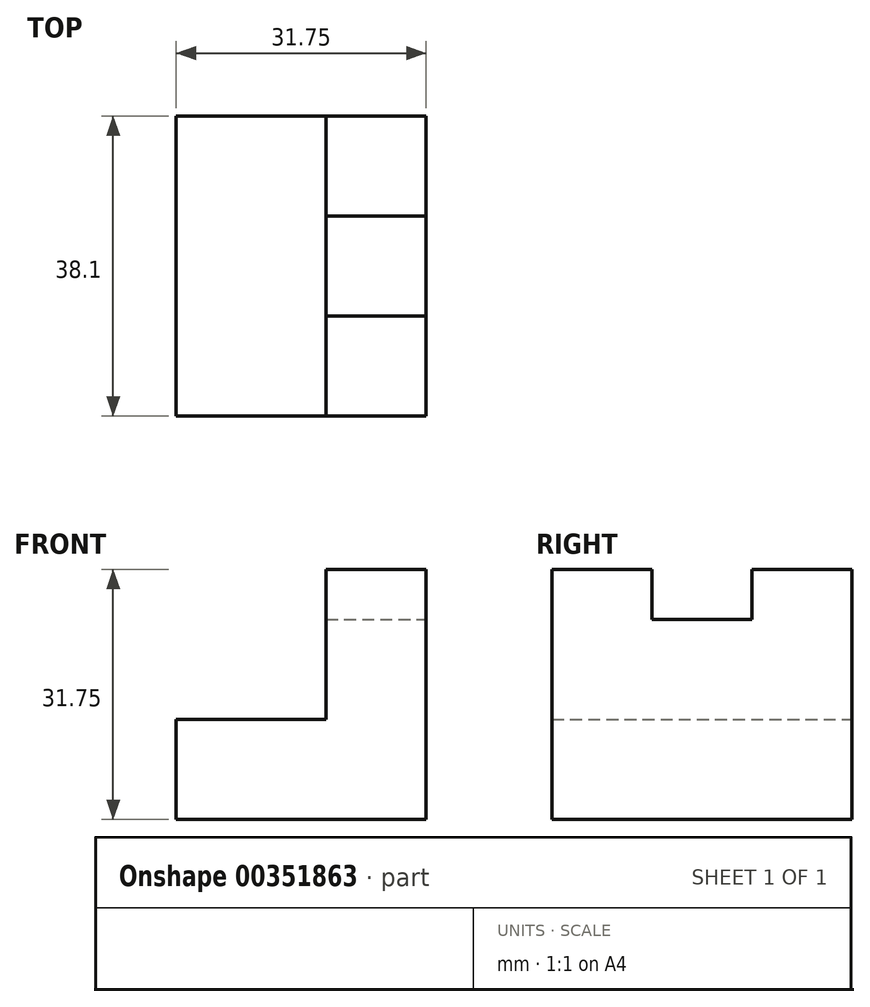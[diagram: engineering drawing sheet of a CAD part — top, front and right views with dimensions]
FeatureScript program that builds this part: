
annotation { "Feature Type Name" : "Feature", "Feature Type Description" : "" }
export const myFeature = defineFeature(function(context is Context, id is Id, definition is map)
    precondition{}
    {
        {
            var Q0;
            Q0=qCreatedBy(makeId("Front.planeOp"),FACE);
            var sketch = newSketch(context, id + "F0", { "sketchPlane" : qUnion([Q0])});
            skLineSegment(sketch, "E0", {"start": v(-41.94, 0) * mm, "end": v(-10.2, 0) * mm});
            skLineSegment(sketch, "E1", {"start": v(-10.2, 0) * mm, "end": v(-10.2, 31.75) * mm});
            skLineSegment(sketch, "E2", {"start": v(-10.2, 31.75) * mm, "end": v(-22.9, 31.75) * mm});
            skLineSegment(sketch, "E3", {"start": v(-22.9, 31.75) * mm, "end": v(-22.9, 12.7) * mm});
            skLineSegment(sketch, "E4", {"start": v(-22.9, 12.7) * mm, "end": v(-41.94, 12.7) * mm});
            skLineSegment(sketch, "E5", {"start": v(-41.94, 12.7) * mm, "end": v(-41.94, 0) * mm});
            skSolve(sketch);
        }
        {
            var Q0;
            Q0 = qSketchRegion(id + "F0", true);
            extrude(context, id + "F1", {"entities" : qUnion([Q0]), "depth" : 38.1 * mm});
        }
        {
            var Q0;
            Q0=makeQuery(id+"F1.opExtrude","SWEPT_FACE",FACE,{"disambiguationData":[OSD([sQuery(id+"F0.wireOp",EDGE,"E1")])]});
            var sketch = newSketch(context, id + "F2", { "sketchPlane" : qUnion([Q0])});
            skLineSegment(sketch, "E6", {"start": v(-25.4, 31.75) * mm, "end": v(-25.4, 25.4) * mm});
            skLineSegment(sketch, "E7", {"start": v(-25.4, 25.4) * mm, "end": v(-12.7, 25.4) * mm});
            skLineSegment(sketch, "E8", {"start": v(-12.7, 25.4) * mm, "end": v(-12.7, 31.75) * mm});
            skSolve(sketch);
        }
        {
            var Q0;
            {var subQ0=sQuery(id+"F2.wireOp",EDGE,"E6");Q0=makeQuery(id+"F2.imprint","IMPRINT",FACE,{"disambiguationData":[TD([[makeQuery(id+"F2.imprint","IMPRINT",EDGE,{"derivedFrom":subQ0}),1.0]])]});}
            extrude(context, id + "F3", {"entities" : qUnion([Q0]), "operationType" : NewBodyOperationType.REMOVE, "oppositeDirection" : true, "depth" : 25.4 * mm});
        }
    });
